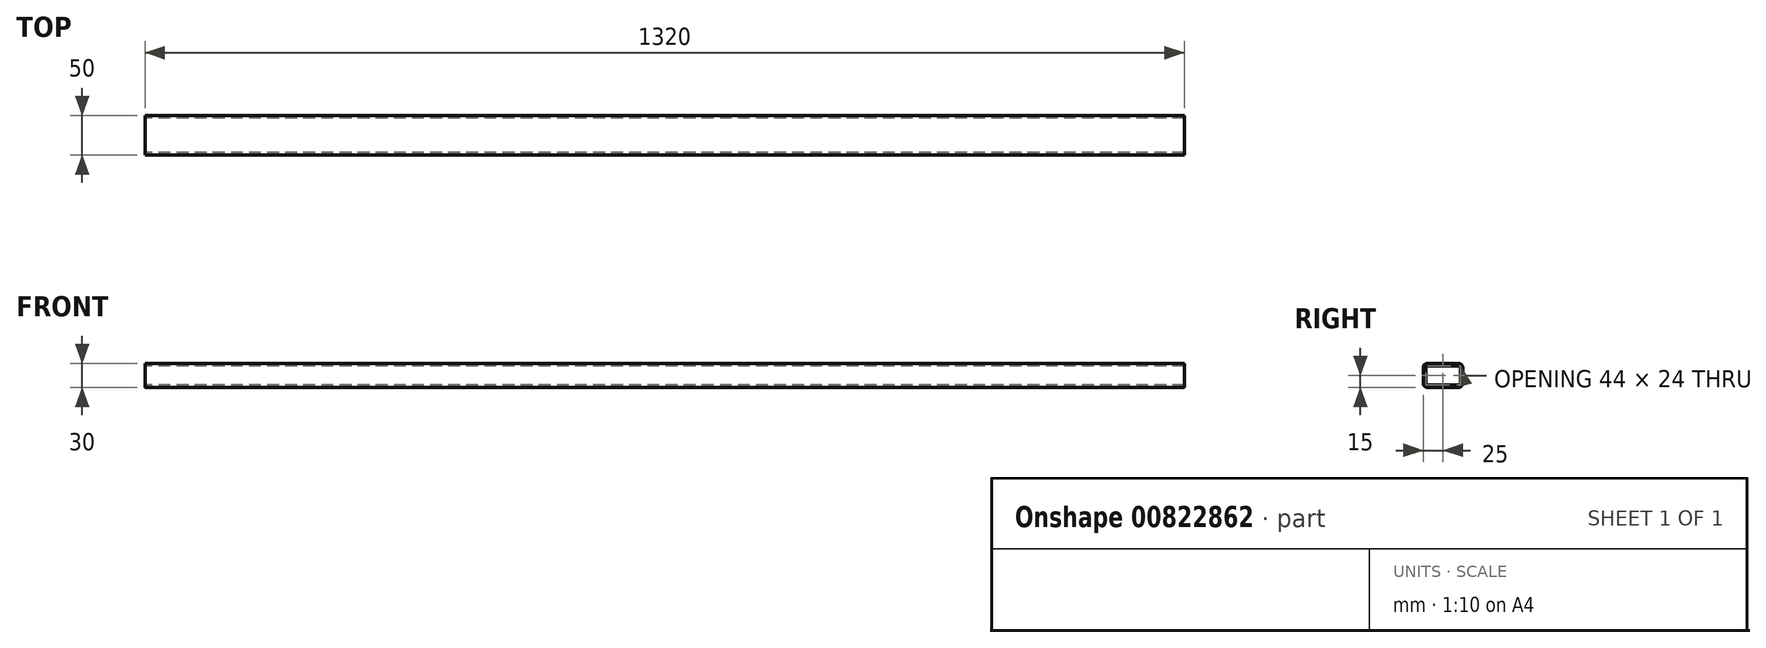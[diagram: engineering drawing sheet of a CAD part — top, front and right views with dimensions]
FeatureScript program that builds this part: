
annotation { "Feature Type Name" : "Feature", "Feature Type Description" : "" }
export const myFeature = defineFeature(function(context is Context, id is Id, definition is map)
    precondition{}
    {
        {
            var Q0;
            Q0=qCreatedBy(makeId("Right.planeOp"),FACE);
            var sketch = newSketch(context, id + "F0", { "sketchPlane" : qUnion([Q0])});
            skLineSegment(sketch, "E0.bottom", {"start": v(-25, -15) * mm, "end": v(25, -15) * mm});
            skLineSegment(sketch, "E0.top", {"start": v(-25, 15) * mm, "end": v(25, 15) * mm});
            skLineSegment(sketch, "E0.left", {"start": v(-25, -15) * mm, "end": v(-25, 15) * mm});
            skLineSegment(sketch, "E0.right", {"start": v(25, -15) * mm, "end": v(25, 15) * mm});
            skPoint(sketch, "E0.middle", {"position": v(0, 0) * mm});
            skLineSegment(sketch, "E1.0", {"start": v(-22, 12) * mm, "end": v(22, 12) * mm});
            skLineSegment(sketch, "E1.1", {"start": v(-22, -12) * mm, "end": v(-22, 12) * mm});
            skLineSegment(sketch, "E1.2", {"start": v(-22, -12) * mm, "end": v(22, -12) * mm});
            skLineSegment(sketch, "E1.3", {"start": v(22, -12) * mm, "end": v(22, 12) * mm});
            skSolve(sketch);
        }
        {
            var Q0;
            Q0 = qSketchRegion(id + "F0", true);
            extrude(context, id + "F1", {"entities" : qUnion([Q0]), "endBound" : BoundingType.SYMMETRIC, "depth" : 1320 * mm, "offsetDistance" : 25 * mm});
        }
        {
            var Q0;
            Q0=makeQuery(id+"F1.opExtrude","SWEPT_EDGE",EDGE,{"disambiguationData":[OSD([sQuery(id+"F0.wireOp",EDGE,"E1.1"),sQuery(id+"F0.wireOp",EDGE,"E1.2")])]});
            var Q1;
            Q1=makeQuery(id+"F1.opExtrude","SWEPT_EDGE",EDGE,{"disambiguationData":[OSD([sQuery(id+"F0.wireOp",EDGE,"E1.0"),sQuery(id+"F0.wireOp",EDGE,"E1.1")])]});
            var Q2;
            Q2=makeQuery(id+"F1.opExtrude","SWEPT_EDGE",EDGE,{"disambiguationData":[OSD([sQuery(id+"F0.wireOp",EDGE,"E1.2"),sQuery(id+"F0.wireOp",EDGE,"E1.3")])]});
            var Q3;
            Q3=makeQuery(id+"F1.opExtrude","SWEPT_EDGE",EDGE,{"disambiguationData":[OSD([sQuery(id+"F0.wireOp",EDGE,"E1.0"),sQuery(id+"F0.wireOp",EDGE,"E1.3")])]});
            fillet(context, id + "F2", {"entities" : qUnion([Q0, Q1, Q2, Q3]), "radius" : 1.5 * mm, "tangentPropagation" : true, "allowEdgeOverflow" : false});
        }
        {
            var Q0;
            Q0=makeQuery(id+"F1.opExtrude","SWEPT_EDGE",EDGE,{"disambiguationData":[OSD([sQuery(id+"F0.wireOp",EDGE,"E0.top"),sQuery(id+"F0.wireOp",EDGE,"E0.left")])]});
            var Q1;
            Q1=makeQuery(id+"F1.opExtrude","SWEPT_EDGE",EDGE,{"disambiguationData":[OSD([sQuery(id+"F0.wireOp",EDGE,"E0.bottom"),sQuery(id+"F0.wireOp",EDGE,"E0.left")])]});
            var Q2;
            Q2=makeQuery(id+"F1.opExtrude","SWEPT_EDGE",EDGE,{"disambiguationData":[OSD([sQuery(id+"F0.wireOp",EDGE,"E0.bottom"),sQuery(id+"F0.wireOp",EDGE,"E0.right")])]});
            var Q3;
            Q3=makeQuery(id+"F1.opExtrude","SWEPT_EDGE",EDGE,{"disambiguationData":[OSD([sQuery(id+"F0.wireOp",EDGE,"E0.top"),sQuery(id+"F0.wireOp",EDGE,"E0.right")])]});
            fillet(context, id + "F3", {"entities" : qUnion([Q0, Q1, Q2, Q3]), "radius" : 4.5 * mm, "tangentPropagation" : true, "allowEdgeOverflow" : false});
        }
    });
